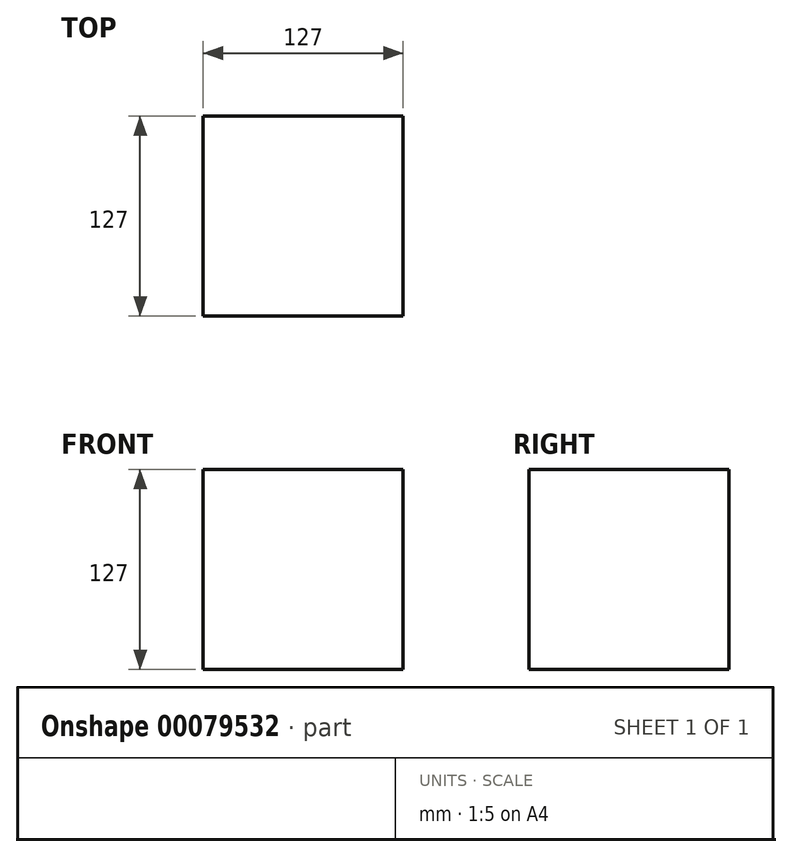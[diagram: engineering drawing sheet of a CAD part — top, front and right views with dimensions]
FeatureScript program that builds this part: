
annotation { "Feature Type Name" : "Feature", "Feature Type Description" : "" }
export const myFeature = defineFeature(function(context is Context, id is Id, definition is map)
    precondition{}
    {
        {
            var Q0;
            Q0=qCreatedBy(makeId("Top.planeOp"),FACE);
            var sketch = newSketch(context, id + "F0", { "sketchPlane" : qUnion([Q0])});
            skLineSegment(sketch, "E0", {"start": v(0, 0) * mm, "end": v(-127, 0) * mm});
            skLineSegment(sketch, "E1", {"start": v(-127, 0) * mm, "end": v(-127, -127) * mm});
            skLineSegment(sketch, "E2", {"start": v(-127, -127) * mm, "end": v(0, -127) * mm});
            skLineSegment(sketch, "E3", {"start": v(0, -127) * mm, "end": v(0, 0) * mm});
            skSolve(sketch);
        }
        {
            var Q0;
            Q0 = qSketchRegion(id + "F0", true);
            extrude(context, id + "F1", {"entities" : qUnion([Q0]), "depth" : 127 * mm});
        }
    });
